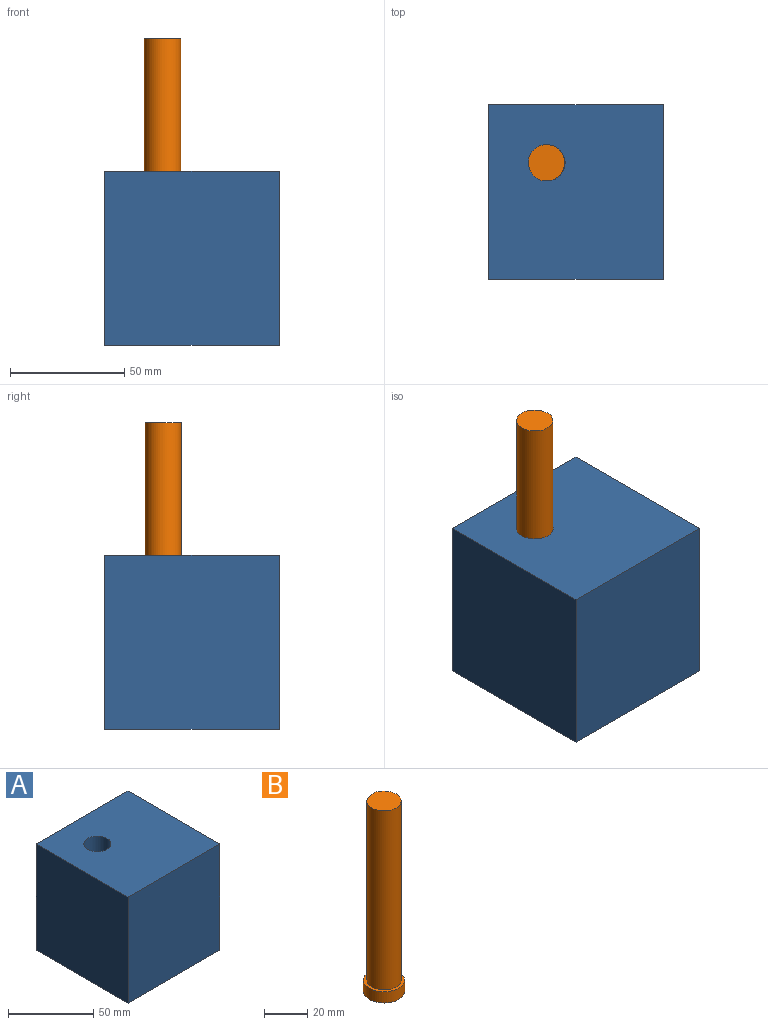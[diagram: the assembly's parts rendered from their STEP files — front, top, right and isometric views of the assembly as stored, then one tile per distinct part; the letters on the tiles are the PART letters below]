
ASSEMBLY  parts=2 mates=1
PART A: 7 faces, bbox 76.2x76.2x76.2 mm
  f0: plane 76.2x76.2mm, normal (0,0,1), area 5608.5mm2, adj f1,f3,f4,f5,f6
  f1: plane 76.2x76.2mm, normal (-1,0,0), area 5806.4mm2, adj f0,f2,f4,f5
  f2: plane 76.2x76.2mm, normal (0,0,-1), area 5608.5mm2, adj f1,f3,f4,f5,f6
  f3: plane 76.2x76.2mm, normal (1,0,0), area 5806.4mm2, adj f0,f2,f4,f5
  f4: plane 76.2x76.2mm, normal (0,-1,0), area 5806.4mm2, adj f0,f1,f2,f3
  f5: plane 76.2x76.2mm, normal (0,1,0), area 5806.4mm2, adj f0,f1,f2,f3
  f6: cylinder r=7.94mm len=76.2mm, axis (0,0,1), area 3800.3mm2, adj f0,f2
PART B: 5 faces, bbox 19.1x19.1x108 mm
  f0: cylinder r=9.53mm len=19.05mm, axis (0,0,-1), area 380mm2, adj f1,f2
  f1: plane 19.05x19.05mm, normal (0,0,1), area 87.1mm2, adj f0,f3
  f2: plane 19.05x19.05mm, normal (0,0,-1), area 285mm2, adj f0
  f3: cylinder r=7.94mm len=101.6mm, axis (0,0,-1), area 5067.1mm2, adj f1,f4
  f4: plane 15.88x15.88mm, normal (0,0,1), area 197.9mm2, adj f3
PLACE A t=(-19.16,-30.53,4.05)mm fixed
PLACE B rot(axis=(0,0,-1),90deg) t=(-59.42,-102.31,-7.35)mm
MATE parallel A.f2 <-> B.f0  axis (0,0,-1) through (-14.62,-69.08,-33.49)mm
